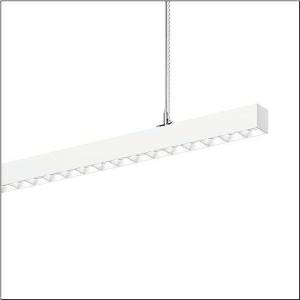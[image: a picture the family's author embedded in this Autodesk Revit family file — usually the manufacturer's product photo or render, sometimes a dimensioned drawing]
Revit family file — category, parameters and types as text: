
# Revit family: silica_r__21_51mx37da47wb_26de
name_source: partatom
category: Lighting Fixtures
units: mm (PartAtom-declared; Revit-internal decimal feet)

## family parameters
Cut with Voids When Loaded = No
Host = Face
Light Source = No
Part Type = Normal
Room Calculation Point = No
Round Connector Dimension = Use Diameter
Shared = No

## types (1)
- --- (1 x LED, 7300 lm, 44 W, 4000K)
    Apparent Load = 44 VA
    CIE Flux Codes = 71 92 99 59 100
    Color Rendering = 80
    Color Temperature = 4000K
    Default Elevation = 1800 mm
    Description = Silica® 21, office luminaire, primary light control with darklight reflector, of PMMA, white, CAT 2 (L<= 3000cd/m²), light emission: direct/indirect distribution, primary light characteristic: asymmetric, installation type: suspended mounting, LED, rated luminous flux: 7.300lm, luminous efficacy: 166lm/W, light colour: 840, colour temperature: 4000K, control gear: DALI 2, with terminal, 3+2-pole, max. 2.5mm², mains connection: 220..240V, AC, 50/60Hz, rated input power: 44W, luminaire housing, of aluminium, traffic white (RAL 9016), length: 1.204mm, width: 53mm, height: 53mm, protection rating (complete): IP20, insulation class (complete): insulation class I (protective earthing), certification: CE, permissible operating ambient temperature: 0..+35°C, standard: EN 50419, packaging unit: 1 piece
    Height = 53 mm
    Lamp = 1 x LED
    Lamp Light Flux = 7300 lm
    Lamp Power = 44 W
    Lamp count = 1
    Length = 1204 mm
    Luminous efficacy = 166 lm/W
    Manufacturer = Siteco
    ModVariant = No
    Model = 51MX37DA47WB
    Mounting Place = Ceiling
    Mounting Type = Pendant
    Number of Poles = 1
    OnlyDefault = Yes
    Power Factor = 1
    Product Name = Silica® 21
    Product group = office luminaire | ceiling pendant
    ProductGroupID = 904
    Protection Class = Protection class I
    Protection Degree = IP 20
    RLX_Detail_Level = 1
    RLX_Emergency_Light_Flux = 0 lm
    RLX_Emergency_Type = 0
    RLX_Emergency_Type_DB = No
    RlxData = <blob elided: 41997 chars, md5=a662cd82>
    Socket = socket
    Standby Power = 0 W
    System Light Flux = 7300 lm
    System Power = 44 W
    Type Comments = factory setting: luminous flux: 100 % | dim-lin: 254 | 368 mA
    Type Image = l_1335921.jpg
    URL = http://relux.com
    VarID = @adj_119674
    Voltage = 0 V
    Weight = 0.00 kg
    Width = 53 mm

## geometry (parser evidence)
native form markers: Blend x4, Sweep x12
no freeform markers — native parametric forms only
